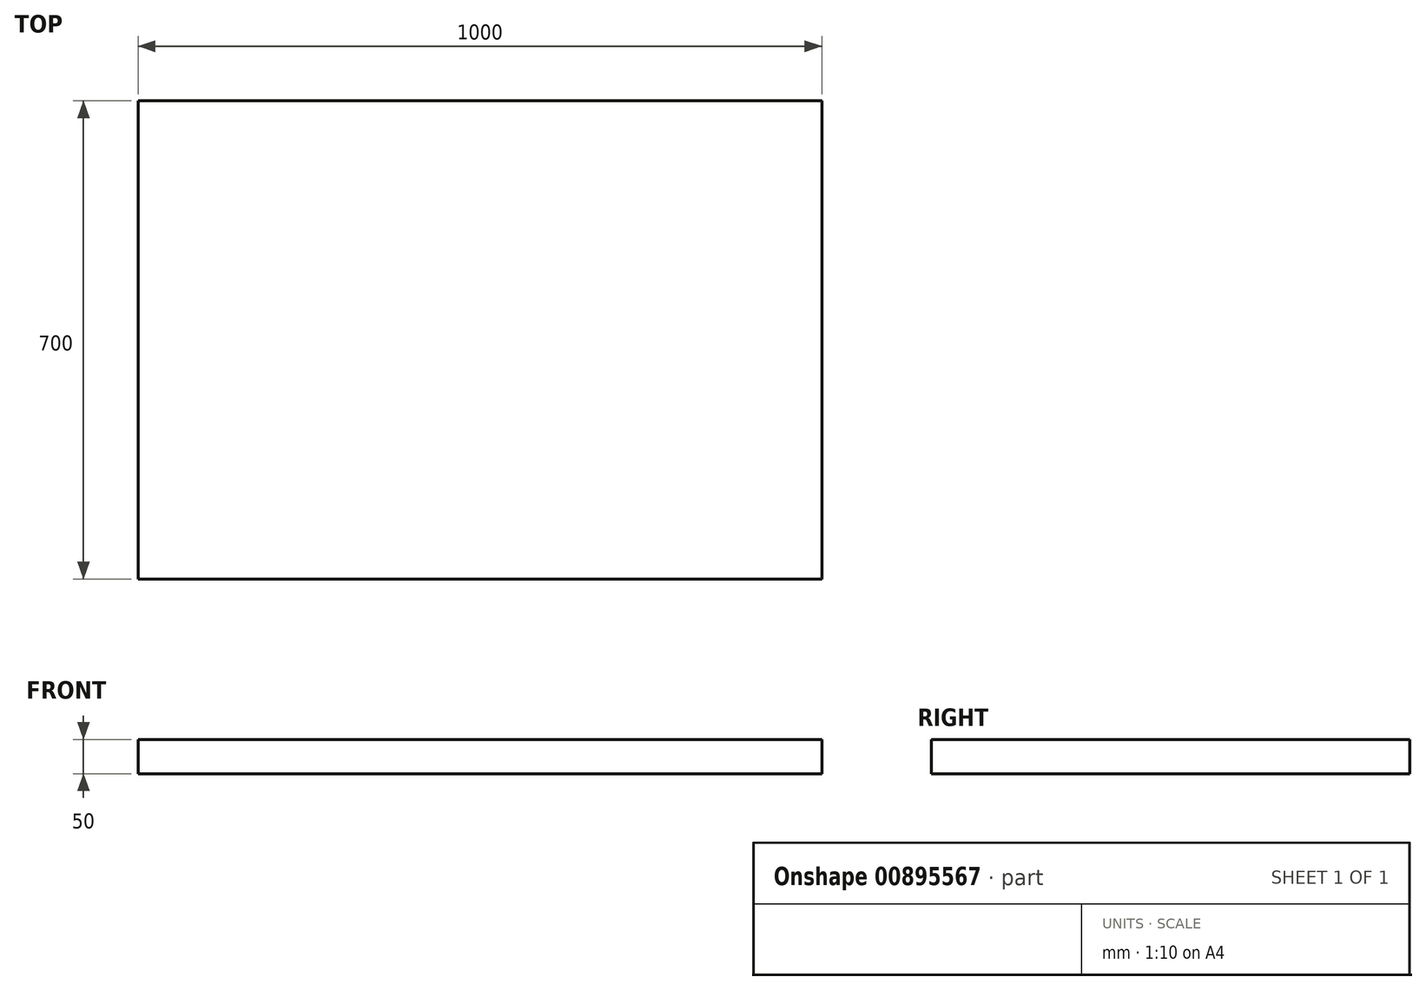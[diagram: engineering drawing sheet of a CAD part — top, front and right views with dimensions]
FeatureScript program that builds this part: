
annotation { "Feature Type Name" : "Feature", "Feature Type Description" : "" }
export const myFeature = defineFeature(function(context is Context, id is Id, definition is map)
    precondition{}
    {
        {
            var Q0;
            Q0=qCreatedBy(makeId("Top.planeOp"),FACE);
            var sketch = newSketch(context, id + "F0", { "sketchPlane" : qUnion([Q0])});
            skLineSegment(sketch, "E0.bottom", {"start": v(-500, 350) * mm, "end": v(500, 350) * mm});
            skLineSegment(sketch, "E0.top", {"start": v(-500, -350) * mm, "end": v(500, -350) * mm});
            skLineSegment(sketch, "E0.left", {"start": v(-500, 350) * mm, "end": v(-500, -350) * mm});
            skLineSegment(sketch, "E0.right", {"start": v(500, 350) * mm, "end": v(500, -350) * mm});
            skPoint(sketch, "E0.middle", {"position": v(0, 0) * mm});
            skSolve(sketch);
        }
        {
            var Q0;
            Q0 = qSketchRegion(id + "F0", true);
            extrude(context, id + "F1", {"entities" : qUnion([Q0]), "depth" : 50 * mm, "offsetDistance" : 25 * mm});
        }
    });
